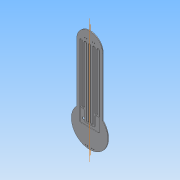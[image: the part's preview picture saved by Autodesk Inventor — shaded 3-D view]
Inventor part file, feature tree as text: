
AUTODESK INVENTOR PART (.ipt)
format: ipt  version: 2013 (Build 170138000, 138)  size: 274,432 bytes
history: native  units: in
note: dims shown in document units (in); Inventor stores cm internally (conversion verified against a paired STEP export)
features: other x5, extrude x3, reference x3, hole x2, sketch x2, plane x1, projected_geometry x1
ambient origin geometry x8: Origin, YZ Plane, XZ Plane, XY Plane, X Axis, Y Axis, Z Axis, Center Point
bodies: Solid1 (feature_tree)
feature tree (17):
  other  "HOT Ply back"
  other  "Blocks"
  extrude  "Extrusion1"  Depth=17.0in
  hole  "Hole Sketch"  [1 undecoded]
  other  "Work Axis1"
  hole  "Hole1"  [1 undecoded]
  extrude  "Extrusion2"  Depth=4.0in
  extrude  "Through Hole"  Depth=1.8125in
  other  "Cut thermo stock"
  plane  "Work Plane1"
  projected_geometry  "Projected Loop1"
  sketch  "Sketch3"  dims[d0=95.5in d2=17.0in]
  other  "One rope curve"
  reference  "Reference1"
  reference  "Reference2"
  reference  "Reference3"
  sketch  "Sketch4"  dims[d3=12.0in d4=0.71in d5=0.0in d8=1.8125in d9=4.0in d10=1.8125in d11=1.8125in d12=0.75in d13=0.75in d14=2.0in d15=15.625in d16=6.302in d17=86.0in d18=0.375in d19=0.75in d20=0.75in d21=0.25in d42=0.5635in d23=1.0in d24=0.8108in d31=52.0in d32=1.24in d33=1.24in d34=0.48in d37=2.5in d39=1.0in d40=1.0in d41=2.0in d43=52.0in d44=1.24in d45=1.24in d46=0.48in d47=52.0in d48=0.48in d49=1.0in d50=62.0in d51=1.24in d52=1.24in d53=0.48in d54=52.0in d55=0.48in d56=1.0in d57=62.0in d58=1.24in d59=1.24in d61=52.0in d62=0.48in d63=1.0in d64=52.0in d65=1.24in d66=1.24in d67=0.48in d68=52.0in d69=0.48in d70=1.0in d71=1.0in d72=0.5in d73=0.0in d74=2.0in d75=2.0in d76=1.0in d77=2.5in d78=1.0in d79=2.25in d80=1.75in d81=0.1875in d82=0.0in d83=0.0in d84=0.0625in]
note: 2 required parameter values undecoded (feature->parameter linkage not recoverable at this tier; creation-order binding heuristic only, values carry confidence <= 0.55)
